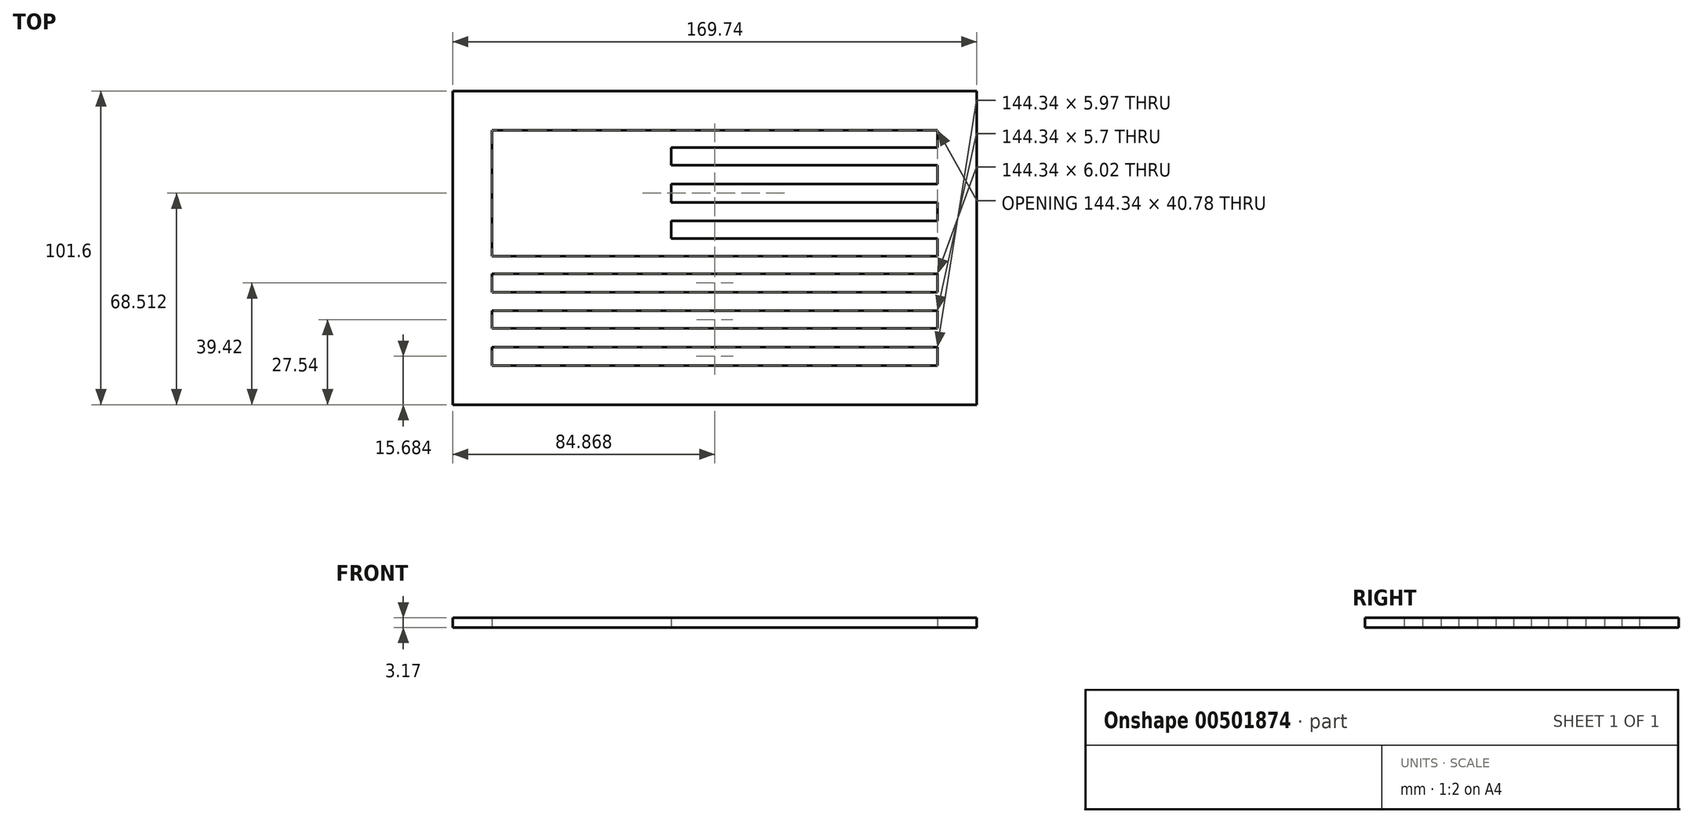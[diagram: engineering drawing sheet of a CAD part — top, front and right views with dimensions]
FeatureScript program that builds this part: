
annotation { "Feature Type Name" : "Feature", "Feature Type Description" : "" }
export const myFeature = defineFeature(function(context is Context, id is Id, definition is map)
    precondition{}
    {
        {
            var Q0;
            Q0=qCreatedBy(makeId("Top.planeOp"),FACE);
            var sketch = newSketch(context, id + "F0", { "sketchPlane" : qUnion([Q0])});
            skLineSegment(sketch, "E0.bottom", {"start": v(0, 0) * mm, "end": v(169.74, 0) * mm});
            skLineSegment(sketch, "E0.top", {"start": v(0, 101.6) * mm, "end": v(169.74, 101.6) * mm});
            skLineSegment(sketch, "E0.left", {"start": v(0, 0) * mm, "end": v(0, 101.6) * mm});
            skLineSegment(sketch, "E0.right", {"start": v(169.74, 0) * mm, "end": v(169.74, 101.6) * mm});
            skLineSegment(sketch, "E1.bottom", {"start": v(12.7, 88.9) * mm, "end": v(157.04, 88.9) * mm});
            skLineSegment(sketch, "E1.top", {"start": v(12.7, 12.7) * mm, "end": v(157.04, 12.7) * mm});
            skLineSegment(sketch, "E1.left", {"start": v(12.7, 88.9) * mm, "end": v(12.7, 12.7) * mm});
            skLineSegment(sketch, "E1.right", {"start": v(157.04, 88.9) * mm, "end": v(157.04, 12.7) * mm});
            skLineSegment(sketch, "E2.bottom", {"start": v(12.7, 88.9) * mm, "end": v(70.78, 88.9) * mm});
            skLineSegment(sketch, "E2.top", {"start": v(12.7, 48.12) * mm, "end": v(70.78, 48.12) * mm});
            skLineSegment(sketch, "E2.left", {"start": v(12.7, 88.9) * mm, "end": v(12.7, 48.12) * mm});
            skLineSegment(sketch, "E2.right", {"start": v(70.78, 88.9) * mm, "end": v(70.78, 48.12) * mm});
            skLineSegment(sketch, "E3.bottom", {"start": v(70.78, 83.24) * mm, "end": v(157.04, 83.24) * mm});
            skLineSegment(sketch, "E3.top", {"start": v(70.78, 77.55) * mm, "end": v(157.04, 77.55) * mm});
            skLineSegment(sketch, "E3.left", {"start": v(70.78, 83.24) * mm, "end": v(70.78, 77.55) * mm});
            skLineSegment(sketch, "E3.right", {"start": v(157.04, 83.24) * mm, "end": v(157.04, 77.55) * mm});
            skLineSegment(sketch, "E4.bottom", {"start": v(70.78, 71.53) * mm, "end": v(157.04, 71.53) * mm});
            skLineSegment(sketch, "E4.top", {"start": v(70.78, 65.5) * mm, "end": v(157.04, 65.5) * mm});
            skLineSegment(sketch, "E4.left", {"start": v(70.78, 71.53) * mm, "end": v(70.78, 65.5) * mm});
            skLineSegment(sketch, "E4.right", {"start": v(157.04, 71.53) * mm, "end": v(157.04, 65.5) * mm});
            skLineSegment(sketch, "E5.bottom", {"start": v(70.78, 59.49) * mm, "end": v(157.04, 59.49) * mm});
            skLineSegment(sketch, "E5.top", {"start": v(70.78, 53.8) * mm, "end": v(157.04, 53.8) * mm});
            skLineSegment(sketch, "E5.left", {"start": v(70.78, 59.49) * mm, "end": v(70.78, 53.8) * mm});
            skLineSegment(sketch, "E5.right", {"start": v(157.04, 59.49) * mm, "end": v(157.04, 53.8) * mm});
            skLineSegment(sketch, "E6.bottom", {"start": v(12.7, 48.12) * mm, "end": v(157.04, 48.12) * mm});
            skLineSegment(sketch, "E6.top", {"start": v(12.7, 42.43) * mm, "end": v(157.04, 42.43) * mm});
            skLineSegment(sketch, "E6.left", {"start": v(12.7, 48.12) * mm, "end": v(12.7, 42.43) * mm});
            skLineSegment(sketch, "E6.right", {"start": v(157.04, 48.12) * mm, "end": v(157.04, 42.43) * mm});
            skLineSegment(sketch, "E7.bottom", {"start": v(12.7, 36.41) * mm, "end": v(157.04, 36.41) * mm});
            skLineSegment(sketch, "E7.top", {"start": v(12.7, 30.4) * mm, "end": v(157.04, 30.4) * mm});
            skLineSegment(sketch, "E7.left", {"start": v(12.7, 36.41) * mm, "end": v(12.7, 30.4) * mm});
            skLineSegment(sketch, "E7.right", {"start": v(157.04, 36.41) * mm, "end": v(157.04, 30.4) * mm});
            skCircle(sketch, "E8.cCircle", {"center": v(17.5, 84.8) * mm, "radius": 1.1 * mm, "construction": true});
            skLineSegment(sketch, "E8.0", {"start": v(18.15, 85.7) * mm, "end": v(18.55, 84.46) * mm});
            skLineSegment(sketch, "E8.1", {"start": v(18.55, 84.46) * mm, "end": v(17.5, 83.7) * mm});
            skLineSegment(sketch, "E8.2", {"start": v(17.5, 83.7) * mm, "end": v(16.46, 84.46) * mm});
            skLineSegment(sketch, "E8.3", {"start": v(16.46, 84.46) * mm, "end": v(16.86, 85.7) * mm});
            skLineSegment(sketch, "E8.4", {"start": v(16.86, 85.7) * mm, "end": v(18.15, 85.7) * mm});
            skLineSegment(sketch, "E9", {"start": v(16.86, 85.7) * mm, "end": v(17.5, 87.69) * mm});
            skLineSegment(sketch, "E10", {"start": v(17.5, 87.69) * mm, "end": v(18.15, 85.7) * mm});
            skLineSegment(sketch, "E11", {"start": v(18.15, 85.7) * mm, "end": v(20.25, 85.7) * mm});
            skLineSegment(sketch, "E12", {"start": v(20.25, 85.7) * mm, "end": v(18.55, 84.46) * mm});
            skLineSegment(sketch, "E13", {"start": v(18.55, 84.46) * mm, "end": v(19.2, 82.46) * mm});
            skLineSegment(sketch, "E14", {"start": v(19.2, 82.46) * mm, "end": v(17.5, 83.7) * mm});
            skLineSegment(sketch, "E15", {"start": v(17.5, 83.7) * mm, "end": v(15.8, 82.46) * mm});
            skLineSegment(sketch, "E16", {"start": v(15.8, 82.46) * mm, "end": v(16.46, 84.46) * mm});
            skLineSegment(sketch, "E17", {"start": v(16.46, 84.46) * mm, "end": v(14.76, 85.7) * mm});
            skLineSegment(sketch, "E18", {"start": v(14.76, 85.7) * mm, "end": v(16.86, 85.7) * mm});
            skLineSegment(sketch, "E19.0.1.0", {"start": v(18.15, 77.56) * mm, "end": v(20.25, 77.56) * mm});
            skLineSegment(sketch, "E19.0.1.1", {"start": v(18.55, 76.33) * mm, "end": v(19.2, 74.34) * mm});
            skLineSegment(sketch, "E19.0.1.2", {"start": v(20.25, 77.56) * mm, "end": v(18.55, 76.33) * mm});
            skLineSegment(sketch, "E19.0.1.3", {"start": v(19.2, 74.34) * mm, "end": v(17.5, 75.57) * mm});
            skLineSegment(sketch, "E19.0.1.4", {"start": v(17.5, 75.57) * mm, "end": v(15.8, 74.34) * mm});
            skLineSegment(sketch, "E19.0.1.5", {"start": v(15.8, 74.34) * mm, "end": v(16.46, 76.33) * mm});
            skLineSegment(sketch, "E19.0.1.6", {"start": v(16.46, 76.33) * mm, "end": v(14.76, 77.56) * mm});
            skLineSegment(sketch, "E19.0.1.7", {"start": v(14.76, 77.56) * mm, "end": v(16.86, 77.56) * mm});
            skLineSegment(sketch, "E19.0.1.8", {"start": v(16.86, 77.56) * mm, "end": v(17.5, 79.56) * mm});
            skLineSegment(sketch, "E19.0.1.9", {"start": v(17.5, 79.56) * mm, "end": v(18.15, 77.56) * mm});
            skLineSegment(sketch, "E19.0.2.0", {"start": v(18.15, 69.44) * mm, "end": v(20.25, 69.44) * mm});
            skLineSegment(sketch, "E19.0.2.1", {"start": v(18.55, 68.2) * mm, "end": v(19.2, 66.2) * mm});
            skLineSegment(sketch, "E19.0.2.2", {"start": v(20.25, 69.44) * mm, "end": v(18.55, 68.2) * mm});
            skLineSegment(sketch, "E19.0.2.3", {"start": v(19.2, 66.2) * mm, "end": v(17.5, 67.44) * mm});
            skLineSegment(sketch, "E19.0.2.4", {"start": v(17.5, 67.44) * mm, "end": v(15.8, 66.2) * mm});
            skLineSegment(sketch, "E19.0.2.5", {"start": v(15.8, 66.2) * mm, "end": v(16.46, 68.2) * mm});
            skLineSegment(sketch, "E19.0.2.6", {"start": v(16.46, 68.2) * mm, "end": v(14.76, 69.44) * mm});
            skLineSegment(sketch, "E19.0.2.7", {"start": v(14.76, 69.44) * mm, "end": v(16.86, 69.44) * mm});
            skLineSegment(sketch, "E19.0.2.8", {"start": v(16.86, 69.44) * mm, "end": v(17.5, 71.43) * mm});
            skLineSegment(sketch, "E19.0.2.9", {"start": v(17.5, 71.43) * mm, "end": v(18.15, 69.44) * mm});
            skLineSegment(sketch, "E19.0.3.0", {"start": v(18.15, 61.3) * mm, "end": v(20.25, 61.3) * mm});
            skLineSegment(sketch, "E19.0.3.1", {"start": v(18.55, 60.08) * mm, "end": v(19.2, 58.08) * mm});
            skLineSegment(sketch, "E19.0.3.2", {"start": v(20.25, 61.3) * mm, "end": v(18.55, 60.08) * mm});
            skLineSegment(sketch, "E19.0.3.3", {"start": v(19.2, 58.08) * mm, "end": v(17.5, 59.31) * mm});
            skLineSegment(sketch, "E19.0.3.4", {"start": v(17.5, 59.31) * mm, "end": v(15.8, 58.08) * mm});
            skLineSegment(sketch, "E19.0.3.5", {"start": v(15.8, 58.08) * mm, "end": v(16.46, 60.08) * mm});
            skLineSegment(sketch, "E19.0.3.6", {"start": v(16.46, 60.08) * mm, "end": v(14.76, 61.3) * mm});
            skLineSegment(sketch, "E19.0.3.7", {"start": v(14.76, 61.3) * mm, "end": v(16.86, 61.3) * mm});
            skLineSegment(sketch, "E19.0.3.8", {"start": v(16.86, 61.3) * mm, "end": v(17.5, 63.3) * mm});
            skLineSegment(sketch, "E19.0.3.9", {"start": v(17.5, 63.3) * mm, "end": v(18.15, 61.3) * mm});
            skLineSegment(sketch, "E19.0.4.0", {"start": v(18.15, 53.18) * mm, "end": v(20.25, 53.18) * mm});
            skLineSegment(sketch, "E19.0.4.1", {"start": v(18.55, 51.95) * mm, "end": v(19.2, 49.95) * mm});
            skLineSegment(sketch, "E19.0.4.2", {"start": v(20.25, 53.18) * mm, "end": v(18.55, 51.95) * mm});
            skLineSegment(sketch, "E19.0.4.3", {"start": v(19.2, 49.95) * mm, "end": v(17.5, 51.19) * mm});
            skLineSegment(sketch, "E19.0.4.4", {"start": v(17.5, 51.19) * mm, "end": v(15.8, 49.95) * mm});
            skLineSegment(sketch, "E19.0.4.5", {"start": v(15.8, 49.95) * mm, "end": v(16.46, 51.95) * mm});
            skLineSegment(sketch, "E19.0.4.6", {"start": v(16.46, 51.95) * mm, "end": v(14.76, 53.18) * mm});
            skLineSegment(sketch, "E19.0.4.7", {"start": v(14.76, 53.18) * mm, "end": v(16.86, 53.18) * mm});
            skLineSegment(sketch, "E19.0.4.8", {"start": v(16.86, 53.18) * mm, "end": v(17.5, 55.17) * mm});
            skLineSegment(sketch, "E19.0.4.9", {"start": v(17.5, 55.17) * mm, "end": v(18.15, 53.18) * mm});
            skLineSegment(sketch, "E19.1.0.0", {"start": v(27.8, 85.7) * mm, "end": v(29.9, 85.7) * mm});
            skLineSegment(sketch, "E19.1.0.1", {"start": v(28.2, 84.46) * mm, "end": v(28.85, 82.46) * mm});
            skLineSegment(sketch, "E19.1.0.2", {"start": v(29.9, 85.7) * mm, "end": v(28.2, 84.46) * mm});
            skLineSegment(sketch, "E19.1.0.3", {"start": v(28.85, 82.46) * mm, "end": v(27.16, 83.7) * mm});
            skLineSegment(sketch, "E19.1.0.4", {"start": v(27.16, 83.7) * mm, "end": v(25.46, 82.46) * mm});
            skLineSegment(sketch, "E19.1.0.5", {"start": v(25.46, 82.46) * mm, "end": v(26.1, 84.46) * mm});
            skLineSegment(sketch, "E19.1.0.6", {"start": v(26.1, 84.46) * mm, "end": v(24.41, 85.7) * mm});
            skLineSegment(sketch, "E19.1.0.7", {"start": v(24.41, 85.7) * mm, "end": v(26.5, 85.7) * mm});
            skLineSegment(sketch, "E19.1.0.8", {"start": v(26.5, 85.7) * mm, "end": v(27.16, 87.69) * mm});
            skLineSegment(sketch, "E19.1.0.9", {"start": v(27.16, 87.69) * mm, "end": v(27.8, 85.7) * mm});
            skLineSegment(sketch, "E19.1.1.0", {"start": v(27.8, 77.56) * mm, "end": v(29.9, 77.56) * mm});
            skLineSegment(sketch, "E19.1.1.1", {"start": v(28.2, 76.33) * mm, "end": v(28.85, 74.34) * mm});
            skLineSegment(sketch, "E19.1.1.2", {"start": v(29.9, 77.56) * mm, "end": v(28.2, 76.33) * mm});
            skLineSegment(sketch, "E19.1.1.3", {"start": v(28.85, 74.34) * mm, "end": v(27.16, 75.57) * mm});
            skLineSegment(sketch, "E19.1.1.4", {"start": v(27.16, 75.57) * mm, "end": v(25.46, 74.34) * mm});
            skLineSegment(sketch, "E19.1.1.5", {"start": v(25.46, 74.34) * mm, "end": v(26.1, 76.33) * mm});
            skLineSegment(sketch, "E19.1.1.6", {"start": v(26.1, 76.33) * mm, "end": v(24.41, 77.56) * mm});
            skLineSegment(sketch, "E19.1.1.7", {"start": v(24.41, 77.56) * mm, "end": v(26.5, 77.56) * mm});
            skLineSegment(sketch, "E19.1.1.8", {"start": v(26.5, 77.56) * mm, "end": v(27.16, 79.56) * mm});
            skLineSegment(sketch, "E19.1.1.9", {"start": v(27.16, 79.56) * mm, "end": v(27.8, 77.56) * mm});
            skLineSegment(sketch, "E19.1.2.0", {"start": v(27.8, 69.44) * mm, "end": v(29.9, 69.44) * mm});
            skLineSegment(sketch, "E19.1.2.1", {"start": v(28.2, 68.2) * mm, "end": v(28.85, 66.2) * mm});
            skLineSegment(sketch, "E19.1.2.2", {"start": v(29.9, 69.44) * mm, "end": v(28.2, 68.2) * mm});
            skLineSegment(sketch, "E19.1.2.3", {"start": v(28.85, 66.2) * mm, "end": v(27.16, 67.44) * mm});
            skLineSegment(sketch, "E19.1.2.4", {"start": v(27.16, 67.44) * mm, "end": v(25.46, 66.2) * mm});
            skLineSegment(sketch, "E19.1.2.5", {"start": v(25.46, 66.2) * mm, "end": v(26.1, 68.2) * mm});
            skLineSegment(sketch, "E19.1.2.6", {"start": v(26.1, 68.2) * mm, "end": v(24.41, 69.44) * mm});
            skLineSegment(sketch, "E19.1.2.7", {"start": v(24.41, 69.44) * mm, "end": v(26.5, 69.44) * mm});
            skLineSegment(sketch, "E19.1.2.8", {"start": v(26.5, 69.44) * mm, "end": v(27.16, 71.43) * mm});
            skLineSegment(sketch, "E19.1.2.9", {"start": v(27.16, 71.43) * mm, "end": v(27.8, 69.44) * mm});
            skLineSegment(sketch, "E19.1.3.0", {"start": v(27.8, 61.3) * mm, "end": v(29.9, 61.3) * mm});
            skLineSegment(sketch, "E19.1.3.1", {"start": v(28.2, 60.08) * mm, "end": v(28.85, 58.08) * mm});
            skLineSegment(sketch, "E19.1.3.2", {"start": v(29.9, 61.3) * mm, "end": v(28.2, 60.08) * mm});
            skLineSegment(sketch, "E19.1.3.3", {"start": v(28.85, 58.08) * mm, "end": v(27.16, 59.31) * mm});
            skLineSegment(sketch, "E19.1.3.4", {"start": v(27.16, 59.31) * mm, "end": v(25.46, 58.08) * mm});
            skLineSegment(sketch, "E19.1.3.5", {"start": v(25.46, 58.08) * mm, "end": v(26.1, 60.08) * mm});
            skLineSegment(sketch, "E19.1.3.6", {"start": v(26.1, 60.08) * mm, "end": v(24.41, 61.3) * mm});
            skLineSegment(sketch, "E19.1.3.7", {"start": v(24.41, 61.3) * mm, "end": v(26.5, 61.3) * mm});
            skLineSegment(sketch, "E19.1.3.8", {"start": v(26.5, 61.3) * mm, "end": v(27.16, 63.3) * mm});
            skLineSegment(sketch, "E19.1.3.9", {"start": v(27.16, 63.3) * mm, "end": v(27.8, 61.3) * mm});
            skLineSegment(sketch, "E19.1.4.0", {"start": v(27.8, 53.18) * mm, "end": v(29.9, 53.18) * mm});
            skLineSegment(sketch, "E19.1.4.1", {"start": v(28.2, 51.95) * mm, "end": v(28.85, 49.95) * mm});
            skLineSegment(sketch, "E19.1.4.2", {"start": v(29.9, 53.18) * mm, "end": v(28.2, 51.95) * mm});
            skLineSegment(sketch, "E19.1.4.3", {"start": v(28.85, 49.95) * mm, "end": v(27.16, 51.19) * mm});
            skLineSegment(sketch, "E19.1.4.4", {"start": v(27.16, 51.19) * mm, "end": v(25.46, 49.95) * mm});
            skLineSegment(sketch, "E19.1.4.5", {"start": v(25.46, 49.95) * mm, "end": v(26.1, 51.95) * mm});
            skLineSegment(sketch, "E19.1.4.6", {"start": v(26.1, 51.95) * mm, "end": v(24.41, 53.18) * mm});
            skLineSegment(sketch, "E19.1.4.7", {"start": v(24.41, 53.18) * mm, "end": v(26.5, 53.18) * mm});
            skLineSegment(sketch, "E19.1.4.8", {"start": v(26.5, 53.18) * mm, "end": v(27.16, 55.17) * mm});
            skLineSegment(sketch, "E19.1.4.9", {"start": v(27.16, 55.17) * mm, "end": v(27.8, 53.18) * mm});
            skLineSegment(sketch, "E19.2.0.0", {"start": v(37.46, 85.7) * mm, "end": v(39.55, 85.7) * mm});
            skLineSegment(sketch, "E19.2.0.1", {"start": v(37.86, 84.46) * mm, "end": v(38.5, 82.46) * mm});
            skLineSegment(sketch, "E19.2.0.2", {"start": v(39.55, 85.7) * mm, "end": v(37.86, 84.46) * mm});
            skLineSegment(sketch, "E19.2.0.3", {"start": v(38.5, 82.46) * mm, "end": v(36.8, 83.7) * mm});
            skLineSegment(sketch, "E19.2.0.4", {"start": v(36.8, 83.7) * mm, "end": v(35.11, 82.46) * mm});
            skLineSegment(sketch, "E19.2.0.5", {"start": v(35.11, 82.46) * mm, "end": v(35.76, 84.46) * mm});
            skLineSegment(sketch, "E19.2.0.6", {"start": v(35.76, 84.46) * mm, "end": v(34.06, 85.7) * mm});
            skLineSegment(sketch, "E19.2.0.7", {"start": v(34.06, 85.7) * mm, "end": v(36.16, 85.7) * mm});
            skLineSegment(sketch, "E19.2.0.8", {"start": v(36.16, 85.7) * mm, "end": v(36.8, 87.69) * mm});
            skLineSegment(sketch, "E19.2.0.9", {"start": v(36.8, 87.69) * mm, "end": v(37.46, 85.7) * mm});
            skLineSegment(sketch, "E19.2.1.0", {"start": v(37.46, 77.56) * mm, "end": v(39.55, 77.56) * mm});
            skLineSegment(sketch, "E19.2.1.1", {"start": v(37.86, 76.33) * mm, "end": v(38.5, 74.34) * mm});
            skLineSegment(sketch, "E19.2.1.2", {"start": v(39.55, 77.56) * mm, "end": v(37.86, 76.33) * mm});
            skLineSegment(sketch, "E19.2.1.3", {"start": v(38.5, 74.34) * mm, "end": v(36.8, 75.57) * mm});
            skLineSegment(sketch, "E19.2.1.4", {"start": v(36.8, 75.57) * mm, "end": v(35.11, 74.34) * mm});
            skLineSegment(sketch, "E19.2.1.5", {"start": v(35.11, 74.34) * mm, "end": v(35.76, 76.33) * mm});
            skLineSegment(sketch, "E19.2.1.6", {"start": v(35.76, 76.33) * mm, "end": v(34.06, 77.56) * mm});
            skLineSegment(sketch, "E19.2.1.7", {"start": v(34.06, 77.56) * mm, "end": v(36.16, 77.56) * mm});
            skLineSegment(sketch, "E19.2.1.8", {"start": v(36.16, 77.56) * mm, "end": v(36.8, 79.56) * mm});
            skLineSegment(sketch, "E19.2.1.9", {"start": v(36.8, 79.56) * mm, "end": v(37.46, 77.56) * mm});
            skLineSegment(sketch, "E19.2.2.0", {"start": v(37.46, 69.44) * mm, "end": v(39.55, 69.44) * mm});
            skLineSegment(sketch, "E19.2.2.1", {"start": v(37.86, 68.2) * mm, "end": v(38.5, 66.2) * mm});
            skLineSegment(sketch, "E19.2.2.2", {"start": v(39.55, 69.44) * mm, "end": v(37.86, 68.2) * mm});
            skLineSegment(sketch, "E19.2.2.3", {"start": v(38.5, 66.2) * mm, "end": v(36.8, 67.44) * mm});
            skLineSegment(sketch, "E19.2.2.4", {"start": v(36.8, 67.44) * mm, "end": v(35.11, 66.2) * mm});
            skLineSegment(sketch, "E19.2.2.5", {"start": v(35.11, 66.2) * mm, "end": v(35.76, 68.2) * mm});
            skLineSegment(sketch, "E19.2.2.6", {"start": v(35.76, 68.2) * mm, "end": v(34.06, 69.44) * mm});
            skLineSegment(sketch, "E19.2.2.7", {"start": v(34.06, 69.44) * mm, "end": v(36.16, 69.44) * mm});
            skLineSegment(sketch, "E19.2.2.8", {"start": v(36.16, 69.44) * mm, "end": v(36.8, 71.43) * mm});
            skLineSegment(sketch, "E19.2.2.9", {"start": v(36.8, 71.43) * mm, "end": v(37.46, 69.44) * mm});
            skLineSegment(sketch, "E19.2.3.0", {"start": v(37.46, 61.3) * mm, "end": v(39.55, 61.3) * mm});
            skLineSegment(sketch, "E19.2.3.1", {"start": v(37.86, 60.08) * mm, "end": v(38.5, 58.08) * mm});
            skLineSegment(sketch, "E19.2.3.2", {"start": v(39.55, 61.3) * mm, "end": v(37.86, 60.08) * mm});
            skLineSegment(sketch, "E19.2.3.3", {"start": v(38.5, 58.08) * mm, "end": v(36.8, 59.31) * mm});
            skLineSegment(sketch, "E19.2.3.4", {"start": v(36.8, 59.31) * mm, "end": v(35.11, 58.08) * mm});
            skLineSegment(sketch, "E19.2.3.5", {"start": v(35.11, 58.08) * mm, "end": v(35.76, 60.08) * mm});
            skLineSegment(sketch, "E19.2.3.6", {"start": v(35.76, 60.08) * mm, "end": v(34.06, 61.3) * mm});
            skLineSegment(sketch, "E19.2.3.7", {"start": v(34.06, 61.3) * mm, "end": v(36.16, 61.3) * mm});
            skLineSegment(sketch, "E19.2.3.8", {"start": v(36.16, 61.3) * mm, "end": v(36.8, 63.3) * mm});
            skLineSegment(sketch, "E19.2.3.9", {"start": v(36.8, 63.3) * mm, "end": v(37.46, 61.3) * mm});
            skLineSegment(sketch, "E19.2.4.0", {"start": v(37.46, 53.18) * mm, "end": v(39.55, 53.18) * mm});
            skLineSegment(sketch, "E19.2.4.1", {"start": v(37.86, 51.95) * mm, "end": v(38.5, 49.95) * mm});
            skLineSegment(sketch, "E19.2.4.2", {"start": v(39.55, 53.18) * mm, "end": v(37.86, 51.95) * mm});
            skLineSegment(sketch, "E19.2.4.3", {"start": v(38.5, 49.95) * mm, "end": v(36.8, 51.19) * mm});
            skLineSegment(sketch, "E19.2.4.4", {"start": v(36.8, 51.19) * mm, "end": v(35.11, 49.95) * mm});
            skLineSegment(sketch, "E19.2.4.5", {"start": v(35.11, 49.95) * mm, "end": v(35.76, 51.95) * mm});
            skLineSegment(sketch, "E19.2.4.6", {"start": v(35.76, 51.95) * mm, "end": v(34.06, 53.18) * mm});
            skLineSegment(sketch, "E19.2.4.7", {"start": v(34.06, 53.18) * mm, "end": v(36.16, 53.18) * mm});
            skLineSegment(sketch, "E19.2.4.8", {"start": v(36.16, 53.18) * mm, "end": v(36.8, 55.17) * mm});
            skLineSegment(sketch, "E19.2.4.9", {"start": v(36.8, 55.17) * mm, "end": v(37.46, 53.18) * mm});
            skLineSegment(sketch, "E19.3.0.0", {"start": v(47.1, 85.7) * mm, "end": v(49.2, 85.7) * mm});
            skLineSegment(sketch, "E19.3.0.1", {"start": v(47.5, 84.46) * mm, "end": v(48.16, 82.46) * mm});
            skLineSegment(sketch, "E19.3.0.2", {"start": v(49.2, 85.7) * mm, "end": v(47.5, 84.46) * mm});
            skLineSegment(sketch, "E19.3.0.3", {"start": v(48.16, 82.46) * mm, "end": v(46.46, 83.7) * mm});
            skLineSegment(sketch, "E19.3.0.4", {"start": v(46.46, 83.7) * mm, "end": v(44.76, 82.46) * mm});
            skLineSegment(sketch, "E19.3.0.5", {"start": v(44.76, 82.46) * mm, "end": v(45.41, 84.46) * mm});
            skLineSegment(sketch, "E19.3.0.6", {"start": v(45.41, 84.46) * mm, "end": v(43.71, 85.7) * mm});
            skLineSegment(sketch, "E19.3.0.7", {"start": v(43.71, 85.7) * mm, "end": v(45.81, 85.7) * mm});
            skLineSegment(sketch, "E19.3.0.8", {"start": v(45.81, 85.7) * mm, "end": v(46.46, 87.69) * mm});
            skLineSegment(sketch, "E19.3.0.9", {"start": v(46.46, 87.69) * mm, "end": v(47.1, 85.7) * mm});
            skLineSegment(sketch, "E19.3.1.0", {"start": v(47.1, 77.56) * mm, "end": v(49.2, 77.56) * mm});
            skLineSegment(sketch, "E19.3.1.1", {"start": v(47.5, 76.33) * mm, "end": v(48.16, 74.34) * mm});
            skLineSegment(sketch, "E19.3.1.2", {"start": v(49.2, 77.56) * mm, "end": v(47.5, 76.33) * mm});
            skLineSegment(sketch, "E19.3.1.3", {"start": v(48.16, 74.34) * mm, "end": v(46.46, 75.57) * mm});
            skLineSegment(sketch, "E19.3.1.4", {"start": v(46.46, 75.57) * mm, "end": v(44.76, 74.34) * mm});
            skLineSegment(sketch, "E19.3.1.5", {"start": v(44.76, 74.34) * mm, "end": v(45.41, 76.33) * mm});
            skLineSegment(sketch, "E19.3.1.6", {"start": v(45.41, 76.33) * mm, "end": v(43.71, 77.56) * mm});
            skLineSegment(sketch, "E19.3.1.7", {"start": v(43.71, 77.56) * mm, "end": v(45.81, 77.56) * mm});
            skLineSegment(sketch, "E19.3.1.8", {"start": v(45.81, 77.56) * mm, "end": v(46.46, 79.56) * mm});
            skLineSegment(sketch, "E19.3.1.9", {"start": v(46.46, 79.56) * mm, "end": v(47.1, 77.56) * mm});
            skLineSegment(sketch, "E19.3.2.0", {"start": v(47.1, 69.44) * mm, "end": v(49.2, 69.44) * mm});
            skLineSegment(sketch, "E19.3.2.1", {"start": v(47.5, 68.2) * mm, "end": v(48.16, 66.2) * mm});
            skLineSegment(sketch, "E19.3.2.2", {"start": v(49.2, 69.44) * mm, "end": v(47.5, 68.2) * mm});
            skLineSegment(sketch, "E19.3.2.3", {"start": v(48.16, 66.2) * mm, "end": v(46.46, 67.44) * mm});
            skLineSegment(sketch, "E19.3.2.4", {"start": v(46.46, 67.44) * mm, "end": v(44.76, 66.2) * mm});
            skLineSegment(sketch, "E19.3.2.5", {"start": v(44.76, 66.2) * mm, "end": v(45.41, 68.2) * mm});
            skLineSegment(sketch, "E19.3.2.6", {"start": v(45.41, 68.2) * mm, "end": v(43.71, 69.44) * mm});
            skLineSegment(sketch, "E19.3.2.7", {"start": v(43.71, 69.44) * mm, "end": v(45.81, 69.44) * mm});
            skLineSegment(sketch, "E19.3.2.8", {"start": v(45.81, 69.44) * mm, "end": v(46.46, 71.43) * mm});
            skLineSegment(sketch, "E19.3.2.9", {"start": v(46.46, 71.43) * mm, "end": v(47.1, 69.44) * mm});
            skLineSegment(sketch, "E19.3.3.0", {"start": v(47.1, 61.3) * mm, "end": v(49.2, 61.3) * mm});
            skLineSegment(sketch, "E19.3.3.1", {"start": v(47.5, 60.08) * mm, "end": v(48.16, 58.08) * mm});
            skLineSegment(sketch, "E19.3.3.2", {"start": v(49.2, 61.3) * mm, "end": v(47.5, 60.08) * mm});
            skLineSegment(sketch, "E19.3.3.3", {"start": v(48.16, 58.08) * mm, "end": v(46.46, 59.31) * mm});
            skLineSegment(sketch, "E19.3.3.4", {"start": v(46.46, 59.31) * mm, "end": v(44.76, 58.08) * mm});
            skLineSegment(sketch, "E19.3.3.5", {"start": v(44.76, 58.08) * mm, "end": v(45.41, 60.08) * mm});
            skLineSegment(sketch, "E19.3.3.6", {"start": v(45.41, 60.08) * mm, "end": v(43.71, 61.3) * mm});
            skLineSegment(sketch, "E19.3.3.7", {"start": v(43.71, 61.3) * mm, "end": v(45.81, 61.3) * mm});
            skLineSegment(sketch, "E19.3.3.8", {"start": v(45.81, 61.3) * mm, "end": v(46.46, 63.3) * mm});
            skLineSegment(sketch, "E19.3.3.9", {"start": v(46.46, 63.3) * mm, "end": v(47.1, 61.3) * mm});
            skLineSegment(sketch, "E19.3.4.0", {"start": v(47.1, 53.18) * mm, "end": v(49.2, 53.18) * mm});
            skLineSegment(sketch, "E19.3.4.1", {"start": v(47.5, 51.95) * mm, "end": v(48.16, 49.95) * mm});
            skLineSegment(sketch, "E19.3.4.2", {"start": v(49.2, 53.18) * mm, "end": v(47.5, 51.95) * mm});
            skLineSegment(sketch, "E19.3.4.3", {"start": v(48.16, 49.95) * mm, "end": v(46.46, 51.19) * mm});
            skLineSegment(sketch, "E19.3.4.4", {"start": v(46.46, 51.19) * mm, "end": v(44.76, 49.95) * mm});
            skLineSegment(sketch, "E19.3.4.5", {"start": v(44.76, 49.95) * mm, "end": v(45.41, 51.95) * mm});
            skLineSegment(sketch, "E19.3.4.6", {"start": v(45.41, 51.95) * mm, "end": v(43.71, 53.18) * mm});
            skLineSegment(sketch, "E19.3.4.7", {"start": v(43.71, 53.18) * mm, "end": v(45.81, 53.18) * mm});
            skLineSegment(sketch, "E19.3.4.8", {"start": v(45.81, 53.18) * mm, "end": v(46.46, 55.17) * mm});
            skLineSegment(sketch, "E19.3.4.9", {"start": v(46.46, 55.17) * mm, "end": v(47.1, 53.18) * mm});
            skLineSegment(sketch, "E19.4.0.0", {"start": v(56.76, 85.7) * mm, "end": v(58.86, 85.7) * mm});
            skLineSegment(sketch, "E19.4.0.1", {"start": v(57.16, 84.46) * mm, "end": v(57.8, 82.46) * mm});
            skLineSegment(sketch, "E19.4.0.2", {"start": v(58.86, 85.7) * mm, "end": v(57.16, 84.46) * mm});
            skLineSegment(sketch, "E19.4.0.3", {"start": v(57.8, 82.46) * mm, "end": v(56.11, 83.7) * mm});
            skLineSegment(sketch, "E19.4.0.4", {"start": v(56.11, 83.7) * mm, "end": v(54.42, 82.46) * mm});
            skLineSegment(sketch, "E19.4.0.5", {"start": v(54.42, 82.46) * mm, "end": v(55.06, 84.46) * mm});
            skLineSegment(sketch, "E19.4.0.6", {"start": v(55.06, 84.46) * mm, "end": v(53.37, 85.7) * mm});
            skLineSegment(sketch, "E19.4.0.7", {"start": v(53.37, 85.7) * mm, "end": v(55.46, 85.7) * mm});
            skLineSegment(sketch, "E19.4.0.8", {"start": v(55.46, 85.7) * mm, "end": v(56.11, 87.69) * mm});
            skLineSegment(sketch, "E19.4.0.9", {"start": v(56.11, 87.69) * mm, "end": v(56.76, 85.7) * mm});
            skLineSegment(sketch, "E19.4.1.0", {"start": v(56.76, 77.56) * mm, "end": v(58.86, 77.56) * mm});
            skLineSegment(sketch, "E19.4.1.1", {"start": v(57.16, 76.33) * mm, "end": v(57.8, 74.34) * mm});
            skLineSegment(sketch, "E19.4.1.2", {"start": v(58.86, 77.56) * mm, "end": v(57.16, 76.33) * mm});
            skLineSegment(sketch, "E19.4.1.3", {"start": v(57.8, 74.34) * mm, "end": v(56.11, 75.57) * mm});
            skLineSegment(sketch, "E19.4.1.4", {"start": v(56.11, 75.57) * mm, "end": v(54.42, 74.34) * mm});
            skLineSegment(sketch, "E19.4.1.5", {"start": v(54.42, 74.34) * mm, "end": v(55.06, 76.33) * mm});
            skLineSegment(sketch, "E19.4.1.6", {"start": v(55.06, 76.33) * mm, "end": v(53.37, 77.56) * mm});
            skLineSegment(sketch, "E19.4.1.7", {"start": v(53.37, 77.56) * mm, "end": v(55.46, 77.56) * mm});
            skLineSegment(sketch, "E19.4.1.8", {"start": v(55.46, 77.56) * mm, "end": v(56.11, 79.56) * mm});
            skLineSegment(sketch, "E19.4.1.9", {"start": v(56.11, 79.56) * mm, "end": v(56.76, 77.56) * mm});
            skLineSegment(sketch, "E19.4.2.0", {"start": v(56.76, 69.44) * mm, "end": v(58.86, 69.44) * mm});
            skLineSegment(sketch, "E19.4.2.1", {"start": v(57.16, 68.2) * mm, "end": v(57.8, 66.2) * mm});
            skLineSegment(sketch, "E19.4.2.2", {"start": v(58.86, 69.44) * mm, "end": v(57.16, 68.2) * mm});
            skLineSegment(sketch, "E19.4.2.3", {"start": v(57.8, 66.2) * mm, "end": v(56.11, 67.44) * mm});
            skLineSegment(sketch, "E19.4.2.4", {"start": v(56.11, 67.44) * mm, "end": v(54.42, 66.2) * mm});
            skLineSegment(sketch, "E19.4.2.5", {"start": v(54.42, 66.2) * mm, "end": v(55.06, 68.2) * mm});
            skLineSegment(sketch, "E19.4.2.6", {"start": v(55.06, 68.2) * mm, "end": v(53.37, 69.44) * mm});
            skLineSegment(sketch, "E19.4.2.7", {"start": v(53.37, 69.44) * mm, "end": v(55.46, 69.44) * mm});
            skLineSegment(sketch, "E19.4.2.8", {"start": v(55.46, 69.44) * mm, "end": v(56.11, 71.43) * mm});
            skLineSegment(sketch, "E19.4.2.9", {"start": v(56.11, 71.43) * mm, "end": v(56.76, 69.44) * mm});
            skLineSegment(sketch, "E19.4.3.0", {"start": v(56.76, 61.3) * mm, "end": v(58.86, 61.3) * mm});
            skLineSegment(sketch, "E19.4.3.1", {"start": v(57.16, 60.08) * mm, "end": v(57.8, 58.08) * mm});
            skLineSegment(sketch, "E19.4.3.2", {"start": v(58.86, 61.3) * mm, "end": v(57.16, 60.08) * mm});
            skLineSegment(sketch, "E19.4.3.3", {"start": v(57.8, 58.08) * mm, "end": v(56.11, 59.31) * mm});
            skLineSegment(sketch, "E19.4.3.4", {"start": v(56.11, 59.31) * mm, "end": v(54.42, 58.08) * mm});
            skLineSegment(sketch, "E19.4.3.5", {"start": v(54.42, 58.08) * mm, "end": v(55.06, 60.08) * mm});
            skLineSegment(sketch, "E19.4.3.6", {"start": v(55.06, 60.08) * mm, "end": v(53.37, 61.3) * mm});
            skLineSegment(sketch, "E19.4.3.7", {"start": v(53.37, 61.3) * mm, "end": v(55.46, 61.3) * mm});
            skLineSegment(sketch, "E19.4.3.8", {"start": v(55.46, 61.3) * mm, "end": v(56.11, 63.3) * mm});
            skLineSegment(sketch, "E19.4.3.9", {"start": v(56.11, 63.3) * mm, "end": v(56.76, 61.3) * mm});
            skLineSegment(sketch, "E19.4.4.0", {"start": v(56.76, 53.18) * mm, "end": v(58.86, 53.18) * mm});
            skLineSegment(sketch, "E19.4.4.1", {"start": v(57.16, 51.95) * mm, "end": v(57.8, 49.95) * mm});
            skLineSegment(sketch, "E19.4.4.2", {"start": v(58.86, 53.18) * mm, "end": v(57.16, 51.95) * mm});
            skLineSegment(sketch, "E19.4.4.3", {"start": v(57.8, 49.95) * mm, "end": v(56.11, 51.19) * mm});
            skLineSegment(sketch, "E19.4.4.4", {"start": v(56.11, 51.19) * mm, "end": v(54.42, 49.95) * mm});
            skLineSegment(sketch, "E19.4.4.5", {"start": v(54.42, 49.95) * mm, "end": v(55.06, 51.95) * mm});
            skLineSegment(sketch, "E19.4.4.6", {"start": v(55.06, 51.95) * mm, "end": v(53.37, 53.18) * mm});
            skLineSegment(sketch, "E19.4.4.7", {"start": v(53.37, 53.18) * mm, "end": v(55.46, 53.18) * mm});
            skLineSegment(sketch, "E19.4.4.8", {"start": v(55.46, 53.18) * mm, "end": v(56.11, 55.17) * mm});
            skLineSegment(sketch, "E19.4.4.9", {"start": v(56.11, 55.17) * mm, "end": v(56.76, 53.18) * mm});
            skLineSegment(sketch, "E19.5.0.0", {"start": v(66.41, 85.7) * mm, "end": v(68.5, 85.7) * mm});
            skLineSegment(sketch, "E19.5.0.1", {"start": v(66.81, 84.46) * mm, "end": v(67.46, 82.46) * mm});
            skLineSegment(sketch, "E19.5.0.2", {"start": v(68.5, 85.7) * mm, "end": v(66.81, 84.46) * mm});
            skLineSegment(sketch, "E19.5.0.3", {"start": v(67.46, 82.46) * mm, "end": v(65.76, 83.7) * mm});
            skLineSegment(sketch, "E19.5.0.4", {"start": v(65.76, 83.7) * mm, "end": v(64.07, 82.46) * mm});
            skLineSegment(sketch, "E19.5.0.5", {"start": v(64.07, 82.46) * mm, "end": v(64.72, 84.46) * mm});
            skLineSegment(sketch, "E19.5.0.6", {"start": v(64.72, 84.46) * mm, "end": v(63.02, 85.7) * mm});
            skLineSegment(sketch, "E19.5.0.7", {"start": v(63.02, 85.7) * mm, "end": v(65.12, 85.7) * mm});
            skLineSegment(sketch, "E19.5.0.8", {"start": v(65.12, 85.7) * mm, "end": v(65.76, 87.69) * mm});
            skLineSegment(sketch, "E19.5.0.9", {"start": v(65.76, 87.69) * mm, "end": v(66.41, 85.7) * mm});
            skLineSegment(sketch, "E19.5.1.0", {"start": v(66.41, 77.56) * mm, "end": v(68.5, 77.56) * mm});
            skLineSegment(sketch, "E19.5.1.1", {"start": v(66.81, 76.33) * mm, "end": v(67.46, 74.34) * mm});
            skLineSegment(sketch, "E19.5.1.2", {"start": v(68.5, 77.56) * mm, "end": v(66.81, 76.33) * mm});
            skLineSegment(sketch, "E19.5.1.3", {"start": v(67.46, 74.34) * mm, "end": v(65.76, 75.57) * mm});
            skLineSegment(sketch, "E19.5.1.4", {"start": v(65.76, 75.57) * mm, "end": v(64.07, 74.34) * mm});
            skLineSegment(sketch, "E19.5.1.5", {"start": v(64.07, 74.34) * mm, "end": v(64.72, 76.33) * mm});
            skLineSegment(sketch, "E19.5.1.6", {"start": v(64.72, 76.33) * mm, "end": v(63.02, 77.56) * mm});
            skLineSegment(sketch, "E19.5.1.7", {"start": v(63.02, 77.56) * mm, "end": v(65.12, 77.56) * mm});
            skLineSegment(sketch, "E19.5.1.8", {"start": v(65.12, 77.56) * mm, "end": v(65.76, 79.56) * mm});
            skLineSegment(sketch, "E19.5.1.9", {"start": v(65.76, 79.56) * mm, "end": v(66.41, 77.56) * mm});
            skLineSegment(sketch, "E19.5.2.0", {"start": v(66.41, 69.44) * mm, "end": v(68.5, 69.44) * mm});
            skLineSegment(sketch, "E19.5.2.1", {"start": v(66.81, 68.2) * mm, "end": v(67.46, 66.2) * mm});
            skLineSegment(sketch, "E19.5.2.2", {"start": v(68.5, 69.44) * mm, "end": v(66.81, 68.2) * mm});
            skLineSegment(sketch, "E19.5.2.3", {"start": v(67.46, 66.2) * mm, "end": v(65.76, 67.44) * mm});
            skLineSegment(sketch, "E19.5.2.4", {"start": v(65.76, 67.44) * mm, "end": v(64.07, 66.2) * mm});
            skLineSegment(sketch, "E19.5.2.5", {"start": v(64.07, 66.2) * mm, "end": v(64.72, 68.2) * mm});
            skLineSegment(sketch, "E19.5.2.6", {"start": v(64.72, 68.2) * mm, "end": v(63.02, 69.44) * mm});
            skLineSegment(sketch, "E19.5.2.7", {"start": v(63.02, 69.44) * mm, "end": v(65.12, 69.44) * mm});
            skLineSegment(sketch, "E19.5.2.8", {"start": v(65.12, 69.44) * mm, "end": v(65.76, 71.43) * mm});
            skLineSegment(sketch, "E19.5.2.9", {"start": v(65.76, 71.43) * mm, "end": v(66.41, 69.44) * mm});
            skLineSegment(sketch, "E19.5.3.0", {"start": v(66.41, 61.3) * mm, "end": v(68.5, 61.3) * mm});
            skLineSegment(sketch, "E19.5.3.1", {"start": v(66.81, 60.08) * mm, "end": v(67.46, 58.08) * mm});
            skLineSegment(sketch, "E19.5.3.2", {"start": v(68.5, 61.3) * mm, "end": v(66.81, 60.08) * mm});
            skLineSegment(sketch, "E19.5.3.3", {"start": v(67.46, 58.08) * mm, "end": v(65.76, 59.31) * mm});
            skLineSegment(sketch, "E19.5.3.4", {"start": v(65.76, 59.31) * mm, "end": v(64.07, 58.08) * mm});
            skLineSegment(sketch, "E19.5.3.5", {"start": v(64.07, 58.08) * mm, "end": v(64.72, 60.08) * mm});
            skLineSegment(sketch, "E19.5.3.6", {"start": v(64.72, 60.08) * mm, "end": v(63.02, 61.3) * mm});
            skLineSegment(sketch, "E19.5.3.7", {"start": v(63.02, 61.3) * mm, "end": v(65.12, 61.3) * mm});
            skLineSegment(sketch, "E19.5.3.8", {"start": v(65.12, 61.3) * mm, "end": v(65.76, 63.3) * mm});
            skLineSegment(sketch, "E19.5.3.9", {"start": v(65.76, 63.3) * mm, "end": v(66.41, 61.3) * mm});
            skLineSegment(sketch, "E19.5.4.0", {"start": v(66.41, 53.18) * mm, "end": v(68.5, 53.18) * mm});
            skLineSegment(sketch, "E19.5.4.1", {"start": v(66.81, 51.95) * mm, "end": v(67.46, 49.95) * mm});
            skLineSegment(sketch, "E19.5.4.2", {"start": v(68.5, 53.18) * mm, "end": v(66.81, 51.95) * mm});
            skLineSegment(sketch, "E19.5.4.3", {"start": v(67.46, 49.95) * mm, "end": v(65.76, 51.19) * mm});
            skLineSegment(sketch, "E19.5.4.4", {"start": v(65.76, 51.19) * mm, "end": v(64.07, 49.95) * mm});
            skLineSegment(sketch, "E19.5.4.5", {"start": v(64.07, 49.95) * mm, "end": v(64.72, 51.95) * mm});
            skLineSegment(sketch, "E19.5.4.6", {"start": v(64.72, 51.95) * mm, "end": v(63.02, 53.18) * mm});
            skLineSegment(sketch, "E19.5.4.7", {"start": v(63.02, 53.18) * mm, "end": v(65.12, 53.18) * mm});
            skLineSegment(sketch, "E19.5.4.8", {"start": v(65.12, 53.18) * mm, "end": v(65.76, 55.17) * mm});
            skLineSegment(sketch, "E19.5.4.9", {"start": v(65.76, 55.17) * mm, "end": v(66.41, 53.18) * mm});
            skLineSegment(sketch, "E19.direction1", {"start": v(15.8, 82.46) * mm, "end": v(25.46, 82.46) * mm, "construction": true});
            skLineSegment(sketch, "E19.direction2", {"start": v(15.8, 82.46) * mm, "end": v(15.8, 74.34) * mm, "construction": true});
            skLineSegment(sketch, "E20.1.0.0", {"start": v(23.12, 81.68) * mm, "end": v(25.22, 81.68) * mm});
            skLineSegment(sketch, "E20.1.0.1", {"start": v(23.52, 80.45) * mm, "end": v(24.17, 78.45) * mm});
            skLineSegment(sketch, "E20.1.0.2", {"start": v(25.22, 81.68) * mm, "end": v(23.52, 80.45) * mm});
            skLineSegment(sketch, "E20.1.0.3", {"start": v(24.17, 78.45) * mm, "end": v(22.47, 79.68) * mm});
            skLineSegment(sketch, "E20.1.0.4", {"start": v(22.47, 79.68) * mm, "end": v(20.78, 78.45) * mm});
            skLineSegment(sketch, "E20.1.0.5", {"start": v(20.78, 78.45) * mm, "end": v(21.42, 80.45) * mm});
            skLineSegment(sketch, "E20.1.0.6", {"start": v(21.42, 80.45) * mm, "end": v(19.73, 81.68) * mm});
            skLineSegment(sketch, "E20.1.0.7", {"start": v(19.73, 81.68) * mm, "end": v(21.82, 81.68) * mm});
            skLineSegment(sketch, "E20.1.0.8", {"start": v(21.82, 81.68) * mm, "end": v(22.47, 83.67) * mm});
            skLineSegment(sketch, "E20.1.0.9", {"start": v(22.47, 83.67) * mm, "end": v(23.12, 81.68) * mm});
            skLineSegment(sketch, "E21.0.1.0", {"start": v(25.22, 73.47) * mm, "end": v(23.52, 72.24) * mm});
            skLineSegment(sketch, "E21.0.1.1", {"start": v(23.12, 73.47) * mm, "end": v(25.22, 73.47) * mm});
            skLineSegment(sketch, "E21.0.1.2", {"start": v(22.47, 75.47) * mm, "end": v(23.12, 73.47) * mm});
            skLineSegment(sketch, "E21.0.1.3", {"start": v(21.82, 73.47) * mm, "end": v(22.47, 75.47) * mm});
            skLineSegment(sketch, "E21.0.1.4", {"start": v(19.73, 73.47) * mm, "end": v(21.82, 73.47) * mm});
            skLineSegment(sketch, "E21.0.1.5", {"start": v(21.42, 72.24) * mm, "end": v(19.73, 73.47) * mm});
            skLineSegment(sketch, "E21.0.1.6", {"start": v(20.78, 70.25) * mm, "end": v(21.42, 72.24) * mm});
            skLineSegment(sketch, "E21.0.1.7", {"start": v(22.47, 71.48) * mm, "end": v(20.78, 70.25) * mm});
            skLineSegment(sketch, "E21.0.1.8", {"start": v(24.17, 70.25) * mm, "end": v(22.47, 71.48) * mm});
            skLineSegment(sketch, "E21.0.1.9", {"start": v(23.52, 72.24) * mm, "end": v(24.17, 70.25) * mm});
            skLineSegment(sketch, "E21.0.2.0", {"start": v(25.22, 65.27) * mm, "end": v(23.52, 64.04) * mm});
            skLineSegment(sketch, "E21.0.2.1", {"start": v(23.12, 65.27) * mm, "end": v(25.22, 65.27) * mm});
            skLineSegment(sketch, "E21.0.2.2", {"start": v(22.47, 67.26) * mm, "end": v(23.12, 65.27) * mm});
            skLineSegment(sketch, "E21.0.2.3", {"start": v(21.82, 65.27) * mm, "end": v(22.47, 67.26) * mm});
            skLineSegment(sketch, "E21.0.2.4", {"start": v(19.73, 65.27) * mm, "end": v(21.82, 65.27) * mm});
            skLineSegment(sketch, "E21.0.2.5", {"start": v(21.42, 64.04) * mm, "end": v(19.73, 65.27) * mm});
            skLineSegment(sketch, "E21.0.2.6", {"start": v(20.78, 62.04) * mm, "end": v(21.42, 64.04) * mm});
            skLineSegment(sketch, "E21.0.2.7", {"start": v(22.47, 63.28) * mm, "end": v(20.78, 62.04) * mm});
            skLineSegment(sketch, "E21.0.2.8", {"start": v(24.17, 62.04) * mm, "end": v(22.47, 63.28) * mm});
            skLineSegment(sketch, "E21.0.2.9", {"start": v(23.52, 64.04) * mm, "end": v(24.17, 62.04) * mm});
            skLineSegment(sketch, "E21.0.3.0", {"start": v(25.22, 57.07) * mm, "end": v(23.52, 55.83) * mm});
            skLineSegment(sketch, "E21.0.3.1", {"start": v(23.12, 57.07) * mm, "end": v(25.22, 57.07) * mm});
            skLineSegment(sketch, "E21.0.3.2", {"start": v(22.47, 59.06) * mm, "end": v(23.12, 57.07) * mm});
            skLineSegment(sketch, "E21.0.3.3", {"start": v(21.82, 57.07) * mm, "end": v(22.47, 59.06) * mm});
            skLineSegment(sketch, "E21.0.3.4", {"start": v(19.73, 57.07) * mm, "end": v(21.82, 57.07) * mm});
            skLineSegment(sketch, "E21.0.3.5", {"start": v(21.42, 55.83) * mm, "end": v(19.73, 57.07) * mm});
            skLineSegment(sketch, "E21.0.3.6", {"start": v(20.78, 53.84) * mm, "end": v(21.42, 55.83) * mm});
            skLineSegment(sketch, "E21.0.3.7", {"start": v(22.47, 55.07) * mm, "end": v(20.78, 53.84) * mm});
            skLineSegment(sketch, "E21.0.3.8", {"start": v(24.17, 53.84) * mm, "end": v(22.47, 55.07) * mm});
            skLineSegment(sketch, "E21.0.3.9", {"start": v(23.52, 55.83) * mm, "end": v(24.17, 53.84) * mm});
            skLineSegment(sketch, "E21.1.0.0", {"start": v(34.72, 81.68) * mm, "end": v(33.02, 80.45) * mm});
            skLineSegment(sketch, "E21.1.0.1", {"start": v(32.62, 81.68) * mm, "end": v(34.72, 81.68) * mm});
            skLineSegment(sketch, "E21.1.0.2", {"start": v(31.97, 83.67) * mm, "end": v(32.62, 81.68) * mm});
            skLineSegment(sketch, "E21.1.0.3", {"start": v(31.32, 81.68) * mm, "end": v(31.97, 83.67) * mm});
            skLineSegment(sketch, "E21.1.0.4", {"start": v(29.23, 81.68) * mm, "end": v(31.32, 81.68) * mm});
            skLineSegment(sketch, "E21.1.0.5", {"start": v(30.92, 80.45) * mm, "end": v(29.23, 81.68) * mm});
            skLineSegment(sketch, "E21.1.0.6", {"start": v(30.28, 78.45) * mm, "end": v(30.92, 80.45) * mm});
            skLineSegment(sketch, "E21.1.0.7", {"start": v(31.97, 79.68) * mm, "end": v(30.28, 78.45) * mm});
            skLineSegment(sketch, "E21.1.0.8", {"start": v(33.67, 78.45) * mm, "end": v(31.97, 79.68) * mm});
            skLineSegment(sketch, "E21.1.0.9", {"start": v(33.02, 80.45) * mm, "end": v(33.67, 78.45) * mm});
            skLineSegment(sketch, "E21.1.1.0", {"start": v(34.72, 73.47) * mm, "end": v(33.02, 72.24) * mm});
            skLineSegment(sketch, "E21.1.1.1", {"start": v(32.62, 73.47) * mm, "end": v(34.72, 73.47) * mm});
            skLineSegment(sketch, "E21.1.1.2", {"start": v(31.97, 75.47) * mm, "end": v(32.62, 73.47) * mm});
            skLineSegment(sketch, "E21.1.1.3", {"start": v(31.32, 73.47) * mm, "end": v(31.97, 75.47) * mm});
            skLineSegment(sketch, "E21.1.1.4", {"start": v(29.23, 73.47) * mm, "end": v(31.32, 73.47) * mm});
            skLineSegment(sketch, "E21.1.1.5", {"start": v(30.92, 72.24) * mm, "end": v(29.23, 73.47) * mm});
            skLineSegment(sketch, "E21.1.1.6", {"start": v(30.28, 70.25) * mm, "end": v(30.92, 72.24) * mm});
            skLineSegment(sketch, "E21.1.1.7", {"start": v(31.97, 71.48) * mm, "end": v(30.28, 70.25) * mm});
            skLineSegment(sketch, "E21.1.1.8", {"start": v(33.67, 70.25) * mm, "end": v(31.97, 71.48) * mm});
            skLineSegment(sketch, "E21.1.1.9", {"start": v(33.02, 72.24) * mm, "end": v(33.67, 70.25) * mm});
            skLineSegment(sketch, "E21.1.2.0", {"start": v(34.72, 65.27) * mm, "end": v(33.02, 64.04) * mm});
            skLineSegment(sketch, "E21.1.2.1", {"start": v(32.62, 65.27) * mm, "end": v(34.72, 65.27) * mm});
            skLineSegment(sketch, "E21.1.2.2", {"start": v(31.97, 67.26) * mm, "end": v(32.62, 65.27) * mm});
            skLineSegment(sketch, "E21.1.2.3", {"start": v(31.32, 65.27) * mm, "end": v(31.97, 67.26) * mm});
            skLineSegment(sketch, "E21.1.2.4", {"start": v(29.23, 65.27) * mm, "end": v(31.32, 65.27) * mm});
            skLineSegment(sketch, "E21.1.2.5", {"start": v(30.92, 64.04) * mm, "end": v(29.23, 65.27) * mm});
            skLineSegment(sketch, "E21.1.2.6", {"start": v(30.28, 62.04) * mm, "end": v(30.92, 64.04) * mm});
            skLineSegment(sketch, "E21.1.2.7", {"start": v(31.97, 63.28) * mm, "end": v(30.28, 62.04) * mm});
            skLineSegment(sketch, "E21.1.2.8", {"start": v(33.67, 62.04) * mm, "end": v(31.97, 63.28) * mm});
            skLineSegment(sketch, "E21.1.2.9", {"start": v(33.02, 64.04) * mm, "end": v(33.67, 62.04) * mm});
            skLineSegment(sketch, "E21.1.3.0", {"start": v(34.72, 57.07) * mm, "end": v(33.02, 55.83) * mm});
            skLineSegment(sketch, "E21.1.3.1", {"start": v(32.62, 57.07) * mm, "end": v(34.72, 57.07) * mm});
            skLineSegment(sketch, "E21.1.3.2", {"start": v(31.97, 59.06) * mm, "end": v(32.62, 57.07) * mm});
            skLineSegment(sketch, "E21.1.3.3", {"start": v(31.32, 57.07) * mm, "end": v(31.97, 59.06) * mm});
            skLineSegment(sketch, "E21.1.3.4", {"start": v(29.23, 57.07) * mm, "end": v(31.32, 57.07) * mm});
            skLineSegment(sketch, "E21.1.3.5", {"start": v(30.92, 55.83) * mm, "end": v(29.23, 57.07) * mm});
            skLineSegment(sketch, "E21.1.3.6", {"start": v(30.28, 53.84) * mm, "end": v(30.92, 55.83) * mm});
            skLineSegment(sketch, "E21.1.3.7", {"start": v(31.97, 55.07) * mm, "end": v(30.28, 53.84) * mm});
            skLineSegment(sketch, "E21.1.3.8", {"start": v(33.67, 53.84) * mm, "end": v(31.97, 55.07) * mm});
            skLineSegment(sketch, "E21.1.3.9", {"start": v(33.02, 55.83) * mm, "end": v(33.67, 53.84) * mm});
            skLineSegment(sketch, "E21.2.0.0", {"start": v(44.22, 81.68) * mm, "end": v(42.52, 80.45) * mm});
            skLineSegment(sketch, "E21.2.0.1", {"start": v(42.12, 81.68) * mm, "end": v(44.22, 81.68) * mm});
            skLineSegment(sketch, "E21.2.0.2", {"start": v(41.47, 83.67) * mm, "end": v(42.12, 81.68) * mm});
            skLineSegment(sketch, "E21.2.0.3", {"start": v(40.82, 81.68) * mm, "end": v(41.47, 83.67) * mm});
            skLineSegment(sketch, "E21.2.0.4", {"start": v(38.73, 81.68) * mm, "end": v(40.82, 81.68) * mm});
            skLineSegment(sketch, "E21.2.0.5", {"start": v(40.42, 80.45) * mm, "end": v(38.73, 81.68) * mm});
            skLineSegment(sketch, "E21.2.0.6", {"start": v(39.78, 78.45) * mm, "end": v(40.42, 80.45) * mm});
            skLineSegment(sketch, "E21.2.0.7", {"start": v(41.47, 79.68) * mm, "end": v(39.78, 78.45) * mm});
            skLineSegment(sketch, "E21.2.0.8", {"start": v(43.17, 78.45) * mm, "end": v(41.47, 79.68) * mm});
            skLineSegment(sketch, "E21.2.0.9", {"start": v(42.52, 80.45) * mm, "end": v(43.17, 78.45) * mm});
            skLineSegment(sketch, "E21.2.1.0", {"start": v(44.22, 73.47) * mm, "end": v(42.52, 72.24) * mm});
            skLineSegment(sketch, "E21.2.1.1", {"start": v(42.12, 73.47) * mm, "end": v(44.22, 73.47) * mm});
            skLineSegment(sketch, "E21.2.1.2", {"start": v(41.47, 75.47) * mm, "end": v(42.12, 73.47) * mm});
            skLineSegment(sketch, "E21.2.1.3", {"start": v(40.82, 73.47) * mm, "end": v(41.47, 75.47) * mm});
            skLineSegment(sketch, "E21.2.1.4", {"start": v(38.73, 73.47) * mm, "end": v(40.82, 73.47) * mm});
            skLineSegment(sketch, "E21.2.1.5", {"start": v(40.42, 72.24) * mm, "end": v(38.73, 73.47) * mm});
            skLineSegment(sketch, "E21.2.1.6", {"start": v(39.78, 70.25) * mm, "end": v(40.42, 72.24) * mm});
            skLineSegment(sketch, "E21.2.1.7", {"start": v(41.47, 71.48) * mm, "end": v(39.78, 70.25) * mm});
            skLineSegment(sketch, "E21.2.1.8", {"start": v(43.17, 70.25) * mm, "end": v(41.47, 71.48) * mm});
            skLineSegment(sketch, "E21.2.1.9", {"start": v(42.52, 72.24) * mm, "end": v(43.17, 70.25) * mm});
            skLineSegment(sketch, "E21.2.2.0", {"start": v(44.22, 65.27) * mm, "end": v(42.52, 64.04) * mm});
            skLineSegment(sketch, "E21.2.2.1", {"start": v(42.12, 65.27) * mm, "end": v(44.22, 65.27) * mm});
            skLineSegment(sketch, "E21.2.2.2", {"start": v(41.47, 67.26) * mm, "end": v(42.12, 65.27) * mm});
            skLineSegment(sketch, "E21.2.2.3", {"start": v(40.82, 65.27) * mm, "end": v(41.47, 67.26) * mm});
            skLineSegment(sketch, "E21.2.2.4", {"start": v(38.73, 65.27) * mm, "end": v(40.82, 65.27) * mm});
            skLineSegment(sketch, "E21.2.2.5", {"start": v(40.42, 64.04) * mm, "end": v(38.73, 65.27) * mm});
            skLineSegment(sketch, "E21.2.2.6", {"start": v(39.78, 62.04) * mm, "end": v(40.42, 64.04) * mm});
            skLineSegment(sketch, "E21.2.2.7", {"start": v(41.47, 63.28) * mm, "end": v(39.78, 62.04) * mm});
            skLineSegment(sketch, "E21.2.2.8", {"start": v(43.17, 62.04) * mm, "end": v(41.47, 63.28) * mm});
            skLineSegment(sketch, "E21.2.2.9", {"start": v(42.52, 64.04) * mm, "end": v(43.17, 62.04) * mm});
            skLineSegment(sketch, "E21.2.3.0", {"start": v(44.22, 57.07) * mm, "end": v(42.52, 55.83) * mm});
            skLineSegment(sketch, "E21.2.3.1", {"start": v(42.12, 57.07) * mm, "end": v(44.22, 57.07) * mm});
            skLineSegment(sketch, "E21.2.3.2", {"start": v(41.47, 59.06) * mm, "end": v(42.12, 57.07) * mm});
            skLineSegment(sketch, "E21.2.3.3", {"start": v(40.82, 57.07) * mm, "end": v(41.47, 59.06) * mm});
            skLineSegment(sketch, "E21.2.3.4", {"start": v(38.73, 57.07) * mm, "end": v(40.82, 57.07) * mm});
            skLineSegment(sketch, "E21.2.3.5", {"start": v(40.42, 55.83) * mm, "end": v(38.73, 57.07) * mm});
            skLineSegment(sketch, "E21.2.3.6", {"start": v(39.78, 53.84) * mm, "end": v(40.42, 55.83) * mm});
            skLineSegment(sketch, "E21.2.3.7", {"start": v(41.47, 55.07) * mm, "end": v(39.78, 53.84) * mm});
            skLineSegment(sketch, "E21.2.3.8", {"start": v(43.17, 53.84) * mm, "end": v(41.47, 55.07) * mm});
            skLineSegment(sketch, "E21.2.3.9", {"start": v(42.52, 55.83) * mm, "end": v(43.17, 53.84) * mm});
            skLineSegment(sketch, "E21.3.0.0", {"start": v(53.72, 81.68) * mm, "end": v(52.02, 80.45) * mm});
            skLineSegment(sketch, "E21.3.0.1", {"start": v(51.62, 81.68) * mm, "end": v(53.72, 81.68) * mm});
            skLineSegment(sketch, "E21.3.0.2", {"start": v(50.97, 83.67) * mm, "end": v(51.62, 81.68) * mm});
            skLineSegment(sketch, "E21.3.0.3", {"start": v(50.32, 81.68) * mm, "end": v(50.97, 83.67) * mm});
            skLineSegment(sketch, "E21.3.0.4", {"start": v(48.23, 81.68) * mm, "end": v(50.32, 81.68) * mm});
            skLineSegment(sketch, "E21.3.0.5", {"start": v(49.92, 80.45) * mm, "end": v(48.23, 81.68) * mm});
            skLineSegment(sketch, "E21.3.0.6", {"start": v(49.27, 78.45) * mm, "end": v(49.92, 80.45) * mm});
            skLineSegment(sketch, "E21.3.0.7", {"start": v(50.97, 79.68) * mm, "end": v(49.27, 78.45) * mm});
            skLineSegment(sketch, "E21.3.0.8", {"start": v(52.67, 78.45) * mm, "end": v(50.97, 79.68) * mm});
            skLineSegment(sketch, "E21.3.0.9", {"start": v(52.02, 80.45) * mm, "end": v(52.67, 78.45) * mm});
            skLineSegment(sketch, "E21.3.1.0", {"start": v(53.72, 73.47) * mm, "end": v(52.02, 72.24) * mm});
            skLineSegment(sketch, "E21.3.1.1", {"start": v(51.62, 73.47) * mm, "end": v(53.72, 73.47) * mm});
            skLineSegment(sketch, "E21.3.1.2", {"start": v(50.97, 75.47) * mm, "end": v(51.62, 73.47) * mm});
            skLineSegment(sketch, "E21.3.1.3", {"start": v(50.32, 73.47) * mm, "end": v(50.97, 75.47) * mm});
            skLineSegment(sketch, "E21.3.1.4", {"start": v(48.23, 73.47) * mm, "end": v(50.32, 73.47) * mm});
            skLineSegment(sketch, "E21.3.1.5", {"start": v(49.92, 72.24) * mm, "end": v(48.23, 73.47) * mm});
            skLineSegment(sketch, "E21.3.1.6", {"start": v(49.27, 70.25) * mm, "end": v(49.92, 72.24) * mm});
            skLineSegment(sketch, "E21.3.1.7", {"start": v(50.97, 71.48) * mm, "end": v(49.27, 70.25) * mm});
            skLineSegment(sketch, "E21.3.1.8", {"start": v(52.67, 70.25) * mm, "end": v(50.97, 71.48) * mm});
            skLineSegment(sketch, "E21.3.1.9", {"start": v(52.02, 72.24) * mm, "end": v(52.67, 70.25) * mm});
            skLineSegment(sketch, "E21.3.2.0", {"start": v(53.72, 65.27) * mm, "end": v(52.02, 64.04) * mm});
            skLineSegment(sketch, "E21.3.2.1", {"start": v(51.62, 65.27) * mm, "end": v(53.72, 65.27) * mm});
            skLineSegment(sketch, "E21.3.2.2", {"start": v(50.97, 67.26) * mm, "end": v(51.62, 65.27) * mm});
            skLineSegment(sketch, "E21.3.2.3", {"start": v(50.32, 65.27) * mm, "end": v(50.97, 67.26) * mm});
            skLineSegment(sketch, "E21.3.2.4", {"start": v(48.23, 65.27) * mm, "end": v(50.32, 65.27) * mm});
            skLineSegment(sketch, "E21.3.2.5", {"start": v(49.92, 64.04) * mm, "end": v(48.23, 65.27) * mm});
            skLineSegment(sketch, "E21.3.2.6", {"start": v(49.27, 62.04) * mm, "end": v(49.92, 64.04) * mm});
            skLineSegment(sketch, "E21.3.2.7", {"start": v(50.97, 63.28) * mm, "end": v(49.27, 62.04) * mm});
            skLineSegment(sketch, "E21.3.2.8", {"start": v(52.67, 62.04) * mm, "end": v(50.97, 63.28) * mm});
            skLineSegment(sketch, "E21.3.2.9", {"start": v(52.02, 64.04) * mm, "end": v(52.67, 62.04) * mm});
            skLineSegment(sketch, "E21.3.3.0", {"start": v(53.72, 57.07) * mm, "end": v(52.02, 55.83) * mm});
            skLineSegment(sketch, "E21.3.3.1", {"start": v(51.62, 57.07) * mm, "end": v(53.72, 57.07) * mm});
            skLineSegment(sketch, "E21.3.3.2", {"start": v(50.97, 59.06) * mm, "end": v(51.62, 57.07) * mm});
            skLineSegment(sketch, "E21.3.3.3", {"start": v(50.32, 57.07) * mm, "end": v(50.97, 59.06) * mm});
            skLineSegment(sketch, "E21.3.3.4", {"start": v(48.23, 57.07) * mm, "end": v(50.32, 57.07) * mm});
            skLineSegment(sketch, "E21.3.3.5", {"start": v(49.92, 55.83) * mm, "end": v(48.23, 57.07) * mm});
            skLineSegment(sketch, "E21.3.3.6", {"start": v(49.27, 53.84) * mm, "end": v(49.92, 55.83) * mm});
            skLineSegment(sketch, "E21.3.3.7", {"start": v(50.97, 55.07) * mm, "end": v(49.27, 53.84) * mm});
            skLineSegment(sketch, "E21.3.3.8", {"start": v(52.67, 53.84) * mm, "end": v(50.97, 55.07) * mm});
            skLineSegment(sketch, "E21.3.3.9", {"start": v(52.02, 55.83) * mm, "end": v(52.67, 53.84) * mm});
            skLineSegment(sketch, "E21.4.0.0", {"start": v(63.22, 81.68) * mm, "end": v(61.52, 80.45) * mm});
            skLineSegment(sketch, "E21.4.0.1", {"start": v(61.12, 81.68) * mm, "end": v(63.22, 81.68) * mm});
            skLineSegment(sketch, "E21.4.0.2", {"start": v(60.47, 83.67) * mm, "end": v(61.12, 81.68) * mm});
            skLineSegment(sketch, "E21.4.0.3", {"start": v(59.82, 81.68) * mm, "end": v(60.47, 83.67) * mm});
            skLineSegment(sketch, "E21.4.0.4", {"start": v(57.73, 81.68) * mm, "end": v(59.82, 81.68) * mm});
            skLineSegment(sketch, "E21.4.0.5", {"start": v(59.42, 80.45) * mm, "end": v(57.73, 81.68) * mm});
            skLineSegment(sketch, "E21.4.0.6", {"start": v(58.77, 78.45) * mm, "end": v(59.42, 80.45) * mm});
            skLineSegment(sketch, "E21.4.0.7", {"start": v(60.47, 79.68) * mm, "end": v(58.77, 78.45) * mm});
            skLineSegment(sketch, "E21.4.0.8", {"start": v(62.17, 78.45) * mm, "end": v(60.47, 79.68) * mm});
            skLineSegment(sketch, "E21.4.0.9", {"start": v(61.52, 80.45) * mm, "end": v(62.17, 78.45) * mm});
            skLineSegment(sketch, "E21.4.1.0", {"start": v(63.22, 73.47) * mm, "end": v(61.52, 72.24) * mm});
            skLineSegment(sketch, "E21.4.1.1", {"start": v(61.12, 73.47) * mm, "end": v(63.22, 73.47) * mm});
            skLineSegment(sketch, "E21.4.1.2", {"start": v(60.47, 75.47) * mm, "end": v(61.12, 73.47) * mm});
            skLineSegment(sketch, "E21.4.1.3", {"start": v(59.82, 73.47) * mm, "end": v(60.47, 75.47) * mm});
            skLineSegment(sketch, "E21.4.1.4", {"start": v(57.73, 73.47) * mm, "end": v(59.82, 73.47) * mm});
            skLineSegment(sketch, "E21.4.1.5", {"start": v(59.42, 72.24) * mm, "end": v(57.73, 73.47) * mm});
            skLineSegment(sketch, "E21.4.1.6", {"start": v(58.77, 70.25) * mm, "end": v(59.42, 72.24) * mm});
            skLineSegment(sketch, "E21.4.1.7", {"start": v(60.47, 71.48) * mm, "end": v(58.77, 70.25) * mm});
            skLineSegment(sketch, "E21.4.1.8", {"start": v(62.17, 70.25) * mm, "end": v(60.47, 71.48) * mm});
            skLineSegment(sketch, "E21.4.1.9", {"start": v(61.52, 72.24) * mm, "end": v(62.17, 70.25) * mm});
            skLineSegment(sketch, "E21.4.2.0", {"start": v(63.22, 65.27) * mm, "end": v(61.52, 64.04) * mm});
            skLineSegment(sketch, "E21.4.2.1", {"start": v(61.12, 65.27) * mm, "end": v(63.22, 65.27) * mm});
            skLineSegment(sketch, "E21.4.2.2", {"start": v(60.47, 67.26) * mm, "end": v(61.12, 65.27) * mm});
            skLineSegment(sketch, "E21.4.2.3", {"start": v(59.82, 65.27) * mm, "end": v(60.47, 67.26) * mm});
            skLineSegment(sketch, "E21.4.2.4", {"start": v(57.73, 65.27) * mm, "end": v(59.82, 65.27) * mm});
            skLineSegment(sketch, "E21.4.2.5", {"start": v(59.42, 64.04) * mm, "end": v(57.73, 65.27) * mm});
            skLineSegment(sketch, "E21.4.2.6", {"start": v(58.77, 62.04) * mm, "end": v(59.42, 64.04) * mm});
            skLineSegment(sketch, "E21.4.2.7", {"start": v(60.47, 63.28) * mm, "end": v(58.77, 62.04) * mm});
            skLineSegment(sketch, "E21.4.2.8", {"start": v(62.17, 62.04) * mm, "end": v(60.47, 63.28) * mm});
            skLineSegment(sketch, "E21.4.2.9", {"start": v(61.52, 64.04) * mm, "end": v(62.17, 62.04) * mm});
            skLineSegment(sketch, "E21.4.3.0", {"start": v(63.22, 57.07) * mm, "end": v(61.52, 55.83) * mm});
            skLineSegment(sketch, "E21.4.3.1", {"start": v(61.12, 57.07) * mm, "end": v(63.22, 57.07) * mm});
            skLineSegment(sketch, "E21.4.3.2", {"start": v(60.47, 59.06) * mm, "end": v(61.12, 57.07) * mm});
            skLineSegment(sketch, "E21.4.3.3", {"start": v(59.82, 57.07) * mm, "end": v(60.47, 59.06) * mm});
            skLineSegment(sketch, "E21.4.3.4", {"start": v(57.73, 57.07) * mm, "end": v(59.82, 57.07) * mm});
            skLineSegment(sketch, "E21.4.3.5", {"start": v(59.42, 55.83) * mm, "end": v(57.73, 57.07) * mm});
            skLineSegment(sketch, "E21.4.3.6", {"start": v(58.77, 53.84) * mm, "end": v(59.42, 55.83) * mm});
            skLineSegment(sketch, "E21.4.3.7", {"start": v(60.47, 55.07) * mm, "end": v(58.77, 53.84) * mm});
            skLineSegment(sketch, "E21.4.3.8", {"start": v(62.17, 53.84) * mm, "end": v(60.47, 55.07) * mm});
            skLineSegment(sketch, "E21.4.3.9", {"start": v(61.52, 55.83) * mm, "end": v(62.17, 53.84) * mm});
            skLineSegment(sketch, "E21.direction1", {"start": v(23.52, 80.45) * mm, "end": v(33.02, 80.45) * mm, "construction": true});
            skLineSegment(sketch, "E21.direction2", {"start": v(23.52, 80.45) * mm, "end": v(23.52, 72.24) * mm, "construction": true});
            skLineSegment(sketch, "E22.bottom", {"start": v(12.7, 24.7) * mm, "end": v(157.04, 24.7) * mm});
            skLineSegment(sketch, "E22.top", {"start": v(12.7, 18.67) * mm, "end": v(157.04, 18.67) * mm});
            skLineSegment(sketch, "E22.left", {"start": v(12.7, 24.7) * mm, "end": v(12.7, 18.67) * mm});
            skLineSegment(sketch, "E22.right", {"start": v(157.04, 24.7) * mm, "end": v(157.04, 18.67) * mm});
            skSolve(sketch);
        }
        {
            var Q0;
            {var subQ4=sQuery(id+"F0.wireOp",EDGE,"E2.bottom");Q0=makeQuery(id+"F0.imprint","IMPRINT",FACE,{"disambiguationData":[TD([[makeQuery(id+"F0.imprint","IMPRINT",EDGE,{"derivedFrom":subQ4}),-1.0]])]});}
            var Q1;
            Q1=makeQuery(id+"F0.imprint","IMPRINT",FACE,{"disambiguationData":[TD([[makeQuery(id+"F0.imprint","IMPRINT",EDGE,{"derivedFrom":sQuery(id+"F0.wireOp",EDGE,"E0.bottom")}),1.0]])]});
            var Q2;
            Q2=makeQuery(id+"F0.imprint","IMPRINT",FACE,{"disambiguationData":[TD([[makeQuery(id+"F0.imprint","IMPRINT",EDGE,{"derivedFrom":sQuery(id+"F0.wireOp",EDGE,"E4.bottom")}),-1.0]])]});
            var Q3;
            Q3=makeQuery(id+"F0.imprint","IMPRINT",FACE,{"disambiguationData":[TD([[makeQuery(id+"F0.imprint","IMPRINT",EDGE,{"derivedFrom":sQuery(id+"F0.wireOp",EDGE,"E5.bottom")}),-1.0]])]});
            var Q4;
            Q4=makeQuery(id+"F0.imprint","IMPRINT",FACE,{"disambiguationData":[TD([[makeQuery(id+"F0.imprint","IMPRINT",EDGE,{"derivedFrom":sQuery(id+"F0.wireOp",EDGE,"E6.top")}),1.0]])]});
            var Q5;
            Q5=makeQuery(id+"F0.imprint","IMPRINT",FACE,{"disambiguationData":[TD([[makeQuery(id+"F0.imprint","IMPRINT",EDGE,{"derivedFrom":sQuery(id+"F0.wireOp",EDGE,"E3.bottom")}),-1.0]])]});
            var Q6;
            Q6=makeQuery(id+"F0.imprint","IMPRINT",FACE,{"disambiguationData":[TD([[makeQuery(id+"F0.imprint","IMPRINT",EDGE,{"derivedFrom":sQuery(id+"F0.wireOp",EDGE,"E7.bottom")}),-1.0]])]});
            var Q7;
            Q7=makeQuery(id+"F0.imprint","IMPRINT",FACE,{"disambiguationData":[TD([[makeQuery(id+"F0.imprint","IMPRINT",EDGE,{"derivedFrom":sQuery(id+"F0.wireOp",EDGE,"E22.bottom")}),-1.0]])]});
            extrude(context, id + "F1", {"entities" : qUnion([Q0, Q1, Q2, Q3, Q4, Q5, Q6, Q7]), "depth" : 3.17 * mm});
        }
    });
